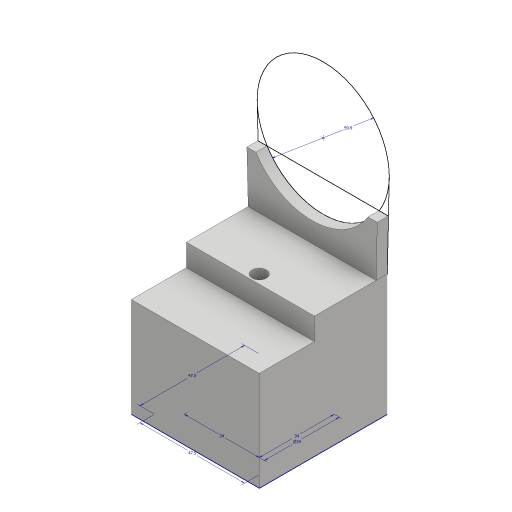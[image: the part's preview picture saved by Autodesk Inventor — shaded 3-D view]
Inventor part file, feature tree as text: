
AUTODESK INVENTOR PART (.ipt)
format: ipt  version: 2023 (Build 270158000, 158)  size: 163,328 bytes
history: native  units: mm
features: hole x4, sketch x3, extrude x3, projected_geometry x1
ambient origin geometry x8: Origin, YZ Plane, XZ Plane, XY Plane, X Axis, Y Axis, Z Axis, Center Point
bodies: Solid1 (feature_tree)
feature tree (11):
  sketch  "Sketch1"  dims[d0=58.0mm d1=58.0mm]
  extrude  "Extrusion1"  Depth=58.0mm
  extrude  "Extrusion2"  Depth=10.0mm TaperAngle=0.0deg
  hole  "Hole1"  [1 undecoded]
  extrude  "Extrusion3"  Depth=5.0mm TaperAngle=0.0deg
  hole  "Hole2"  [1 undecoded]
  hole  "Hole3"  [1 undecoded]
  hole  "Hole4"  [1 undecoded]
  sketch  "Sketch2"  dims[d2=55.066mm d3=0.0mm d4=10.0mm d5=0.0mm]
  sketch  "Sketch3"  dims[d6=6.5mm d7=6.0mm d8=4.0mm d9=2.0mm d10=90.0deg d11=8.0mm d12=20.594885mm d13=59.9mm d14=5.0mm d15=0.0mm d16=6.756mm d17=12.0mm d18=11.113mm d19=11.0mm d20=90.0deg d21=13.0mm d22=20.594885mm d23=47.5mm d24=47.5mm d25=2.459mm d26=6.0mm d27=11.113mm d28=6.35mm d29=90.0deg d30=8.8mm d31=20.594885mm d33=34.0mm d34=20.0mm d36=34.0mm d37=20.0mm d39=34.0mm d42=3.242mm d43=8.0mm d44=11.113mm d45=11.0mm d46=14.3117mm d47=11.8mm d48=20.594885mm]
  projected_geometry  "Projected Loop1"
note: 4 required parameter values undecoded (feature->parameter linkage not recoverable at this tier; creation-order binding heuristic only, values carry confidence <= 0.55)
